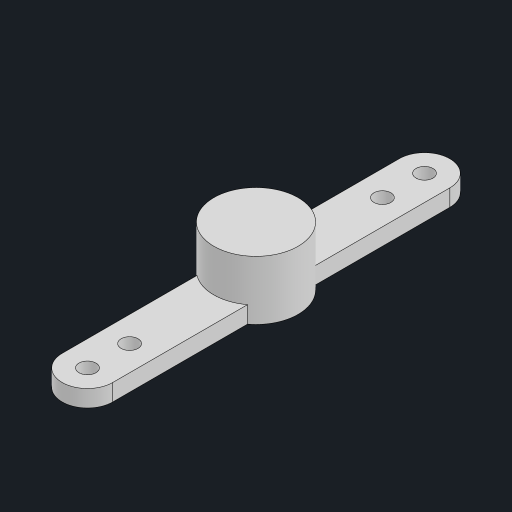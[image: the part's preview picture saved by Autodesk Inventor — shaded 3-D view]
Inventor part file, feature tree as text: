
AUTODESK INVENTOR PART (.ipt)
format: ipt  version: 2023 (Build 270158000, 158)  size: 122,368 bytes
history: native  units: in
note: dims shown in document units (in); Inventor stores cm internally (conversion verified against a paired STEP export)
features: sketch x3, extrude x2, other x1, hole x1
ambient origin geometry x8: Origin, YZ Plane, XZ Plane, XY Plane, X Axis, Y Axis, Z Axis, Center Point
bodies: Body1 (feature_tree)
feature tree (7):
  other  "ソリッド1"
  sketch  "スケッチ1"
  extrude  "押し出し1"  Depth=0.1969in
  extrude  "押し出し2"  Depth=0.1181in
  hole  "穴1"  [1 undecoded]
  sketch  "スケッチ2"
  sketch  "スケッチ3"
note: 1 required parameter value undecoded (feature->parameter linkage not recoverable at this tier; creation-order binding heuristic only, values carry confidence <= 0.55)
